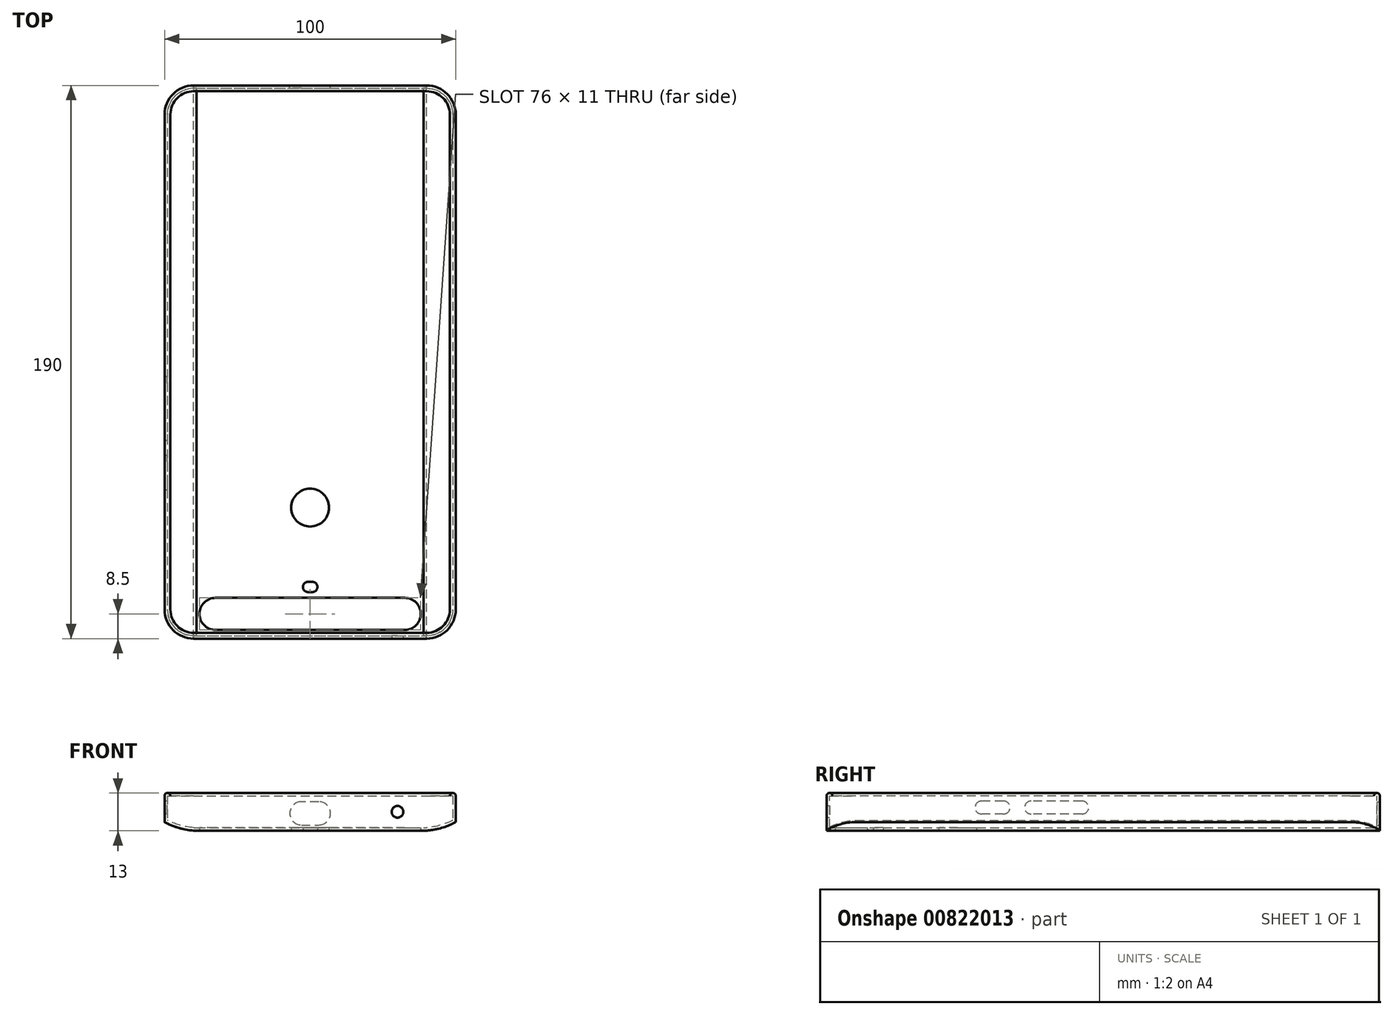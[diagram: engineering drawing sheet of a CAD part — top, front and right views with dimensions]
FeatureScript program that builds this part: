
annotation { "Feature Type Name" : "Feature", "Feature Type Description" : "" }
export const myFeature = defineFeature(function(context is Context, id is Id, definition is map)
    precondition{}
    {
        {
            var Q0;
            Q0=qCreatedBy(makeId("Top.planeOp"),FACE);
            var sketch = newSketch(context, id + "F0", { "sketchPlane" : qUnion([Q0])});
            skLineSegment(sketch, "E0.bottom", {"start": v(-40, 95) * mm, "end": v(40, 95) * mm});
            skLineSegment(sketch, "E0.top", {"start": v(-40, -95) * mm, "end": v(40, -95) * mm});
            skLineSegment(sketch, "E0.left", {"start": v(-50, 85) * mm, "end": v(-50, -85) * mm});
            skLineSegment(sketch, "E0.right", {"start": v(50, 85) * mm, "end": v(50, -85) * mm});
            skPoint(sketch, "E1.visualSharp", {"position": v(-50, 95) * mm});
            skArc(sketch, "E1.filletArc", {"start": v(-40, 95) * mm, "mid": v(-47.07, 92.07) * mm, "end": v(-50, 85) * mm});
            skPoint(sketch, "E2.visualSharp", {"position": v(50, 95) * mm});
            skArc(sketch, "E2.filletArc", {"start": v(50, 85) * mm, "mid": v(47.07, 92.07) * mm, "end": v(40, 95) * mm});
            skPoint(sketch, "E3.visualSharp", {"position": v(50, -95) * mm});
            skArc(sketch, "E3.filletArc", {"start": v(40, -95) * mm, "mid": v(47.07, -92.07) * mm, "end": v(50, -85) * mm});
            skPoint(sketch, "E4.visualSharp", {"position": v(-50, -95) * mm});
            skArc(sketch, "E4.filletArc", {"start": v(-50, -85) * mm, "mid": v(-47.07, -92.07) * mm, "end": v(-40, -95) * mm});
            skLineSegment(sketch, "E5", {"start": v(0, 95) * mm, "end": v(0, -95) * mm, "construction": true});
            skLineSegment(sketch, "E6", {"start": v(-50, 0) * mm, "end": v(50, 0) * mm, "construction": true});
            skSolve(sketch);
        }
        {
            var Q0;
            Q0=makeQuery(id+"F0.imprint","IMPRINT",FACE,{"disambiguationData":[TD([[makeQuery(id+"F0.imprint","IMPRINT",EDGE,{"derivedFrom":sQuery(id+"F0.wireOp",EDGE,"E0.bottom")}),-1.0]])]});
            extrude(context, id + "F1", {"entities" : qUnion([Q0]), "depth" : 12 * mm});
        }
        {
            var Q0;
            Q0=makeQuery(id+"F1.opExtrude","SWEPT_FACE",FACE,{"disambiguationData":[OSD([sQuery(id+"F0.wireOp",EDGE,"E0.bottom")])]});
            var sketch = newSketch(context, id + "F2", { "sketchPlane" : qUnion([Q0])});
            skLineSegment(sketch, "E7.0", {"start": v(-50, 0) * mm, "end": v(-38, 0) * mm});
            skLineSegment(sketch, "E8.0", {"start": v(-50, 3) * mm, "end": v(-50, 0) * mm});
            skArc(sketch, "E9", {"start": v(-50, 3) * mm, "mid": v(-44.19, 0.75) * mm, "end": v(-38, 0) * mm});
            skArc(sketch, "E10.MirrorCS", {"start": v(50, 3) * mm, "mid": v(44.19, 0.75) * mm, "end": v(38, 0) * mm});
            skLineSegment(sketch, "E11.MirrorCS", {"start": v(50, 3) * mm, "end": v(50, 0) * mm});
            skLineSegment(sketch, "E12.MirrorCS", {"start": v(50, 0) * mm, "end": v(38, 0) * mm});
            skSolve(sketch);
        }
        {
            var Q0;
            {var subQ3=sQuery(id+"F2.wireOp",EDGE,"E8.0");Q0=makeQuery(id+"F2.imprint","IMPRINT",FACE,{"disambiguationData":[TD([[makeQuery(id+"F2.imprint","IMPRINT",EDGE,{"derivedFrom":subQ3}),1.0]])]});}
            var Q1;
            {var subQ0=sQuery(id+"F2.wireOp",EDGE,"E11.MirrorCS");Q1=makeQuery(id+"F2.imprint","IMPRINT",FACE,{"disambiguationData":[TD([[makeQuery(id+"F2.imprint","IMPRINT",EDGE,{"derivedFrom":subQ0}),-1.0]])]});}
            extrude(context, id + "F3", {"entities" : qUnion([Q0, Q1]), "operationType" : NewBodyOperationType.REMOVE, "endBound" : BoundingType.THROUGH_ALL, "oppositeDirection" : true, "depth" : 25 * mm});
        }
        {
            var Q0;
            Q0=makeQuery(id+"F1.opExtrude","CAP_FACE",FACE,{"disambiguationData":[OSD([sQuery(id+"F0.wireOp",EDGE,"E0.bottom"),sQuery(id+"F0.wireOp",EDGE,"E0.top"),sQuery(id+"F0.wireOp",EDGE,"E0.left"),sQuery(id+"F0.wireOp",EDGE,"E0.right"),sQuery(id+"F0.wireOp",EDGE,"E1.filletArc"),sQuery(id+"F0.wireOp",EDGE,"E2.filletArc"),sQuery(id+"F0.wireOp",EDGE,"E3.filletArc"),sQuery(id+"F0.wireOp",EDGE,"E4.filletArc")])],"isStart":false});
            shell(context, id + "F4", {"entities" : qUnion([Q0]), "thickness" : 1 * mm});
        }
        {
            var Q0;
            Q0=makeQuery(id+"F1.opExtrude","CAP_FACE",FACE,{"disambiguationData":[OSD([sQuery(id+"F0.wireOp",EDGE,"E0.bottom"),sQuery(id+"F0.wireOp",EDGE,"E0.top"),sQuery(id+"F0.wireOp",EDGE,"E0.left"),sQuery(id+"F0.wireOp",EDGE,"E0.right"),sQuery(id+"F0.wireOp",EDGE,"E1.filletArc"),sQuery(id+"F0.wireOp",EDGE,"E2.filletArc"),sQuery(id+"F0.wireOp",EDGE,"E3.filletArc"),sQuery(id+"F0.wireOp",EDGE,"E4.filletArc")])],"isStart":false});
            var sketch = newSketch(context, id + "F5", { "sketchPlane" : qUnion([Q0])});
            skLineSegment(sketch, "E13.0", {"start": v(-40, 95) * mm, "end": v(40, 95) * mm});
            skArc(sketch, "E14.0", {"start": v(-40, 95) * mm, "mid": v(-47.07, 92.07) * mm, "end": v(-50, 85) * mm});
            skLineSegment(sketch, "E15.0", {"start": v(-50, 85) * mm, "end": v(-50, -85) * mm});
            skArc(sketch, "E16.0", {"start": v(50, 85) * mm, "mid": v(47.07, 92.07) * mm, "end": v(40, 95) * mm});
            skLineSegment(sketch, "E17.0", {"start": v(50, 85) * mm, "end": v(50, -85) * mm});
            skArc(sketch, "E18.0", {"start": v(-50, -85) * mm, "mid": v(-47.07, -92.07) * mm, "end": v(-40, -95) * mm});
            skLineSegment(sketch, "E19.0", {"start": v(-40, -95) * mm, "end": v(40, -95) * mm});
            skArc(sketch, "E20.0", {"start": v(40, -95) * mm, "mid": v(47.07, -92.07) * mm, "end": v(50, -85) * mm});
            skLineSegment(sketch, "E21.0", {"start": v(-40, 93) * mm, "end": v(40, 93) * mm});
            skArc(sketch, "E21.1", {"start": v(48, 85) * mm, "mid": v(45.66, 90.66) * mm, "end": v(40, 93) * mm});
            skArc(sketch, "E21.2", {"start": v(-40, 93) * mm, "mid": v(-45.66, 90.66) * mm, "end": v(-48, 85) * mm});
            skLineSegment(sketch, "E21.3", {"start": v(48, 85) * mm, "end": v(48, -85) * mm});
            skLineSegment(sketch, "E21.4", {"start": v(-48, 85) * mm, "end": v(-48, -85) * mm});
            skArc(sketch, "E21.5", {"start": v(-48, -85) * mm, "mid": v(-45.66, -90.66) * mm, "end": v(-40, -93) * mm});
            skLineSegment(sketch, "E21.6", {"start": v(-40, -93) * mm, "end": v(40, -93) * mm});
            skArc(sketch, "E21.7", {"start": v(40, -93) * mm, "mid": v(45.66, -90.66) * mm, "end": v(48, -85) * mm});
            skSolve(sketch);
        }
        {
            var Q0;
            Q0=qSketchRegion(id+"F5",true);
            extrude(context, id + "F6", {"entities" : qUnion([Q0]), "operationType" : NewBodyOperationType.ADD, "depth" : 1 * mm});
        }
        {
            var Q0;
            Q0=makeQuery(id+"F1.opExtrude","CAP_FACE",FACE,{"disambiguationData":[OSD([sQuery(id+"F0.wireOp",EDGE,"E0.bottom"),sQuery(id+"F0.wireOp",EDGE,"E0.top"),sQuery(id+"F0.wireOp",EDGE,"E0.left"),sQuery(id+"F0.wireOp",EDGE,"E0.right"),sQuery(id+"F0.wireOp",EDGE,"E1.filletArc"),sQuery(id+"F0.wireOp",EDGE,"E2.filletArc"),sQuery(id+"F0.wireOp",EDGE,"E3.filletArc"),sQuery(id+"F0.wireOp",EDGE,"E4.filletArc")])],"isStart":true});
            var sketch = newSketch(context, id + "F7", { "sketchPlane" : qUnion([Q0])});
            skLineSegment(sketch, "E22", {"start": v(-40, 95) * mm, "end": v(-40, -95) * mm, "construction": true});
            skLineSegment(sketch, "E23", {"start": v(40, 95) * mm, "end": v(40, -95) * mm, "construction": true});
            skCircle(sketch, "E24", {"center": v(0, 50) * mm, "radius": 6.5 * mm});
            skLineSegment(sketch, "E25", {"start": v(-38, 92) * mm, "end": v(-32.5, 92) * mm, "construction": true});
            skLineSegment(sketch, "E26", {"start": v(-38, 81) * mm, "end": v(-32.5, 81) * mm, "construction": true});
            skLineSegment(sketch, "E27", {"start": v(0, 79) * mm, "end": v(0, 95) * mm, "construction": true});
            skArc(sketch, "E28", {"start": v(-32.5, 92) * mm, "mid": v(-38, 86.5) * mm, "end": v(-32.5, 81) * mm});
            skArc(sketch, "E29", {"start": v(32.5, 81) * mm, "mid": v(38, 86.5) * mm, "end": v(32.5, 92) * mm});
            skLineSegment(sketch, "E30", {"start": v(38, 92) * mm, "end": v(38, 81) * mm, "construction": true});
            skLineSegment(sketch, "E31", {"start": v(-38, 92) * mm, "end": v(-38, 81) * mm, "construction": true});
            skLineSegment(sketch, "E32", {"start": v(-32.5, 92) * mm, "end": v(32.5, 92) * mm});
            skLineSegment(sketch, "E33", {"start": v(32.5, 81) * mm, "end": v(-32.5, 81) * mm});
            skLineSegment(sketch, "E34.trimOffspring", {"start": v(32.5, 92) * mm, "end": v(38, 92) * mm, "construction": true});
            skLineSegment(sketch, "E35.trimOffspring", {"start": v(32.5, 81) * mm, "end": v(38, 81) * mm, "construction": true});
            skLineSegment(sketch, "E36", {"start": v(-2.5, 79) * mm, "end": v(-0.75, 79) * mm, "construction": true});
            skLineSegment(sketch, "E37", {"start": v(-2.5, 75.5) * mm, "end": v(-0.75, 75.5) * mm, "construction": true});
            skLineSegment(sketch, "E38", {"start": v(-2.5, 79) * mm, "end": v(-2.5, 75.5) * mm, "construction": true});
            skLineSegment(sketch, "E39", {"start": v(2.5, 79) * mm, "end": v(2.5, 75.5) * mm, "construction": true});
            skArc(sketch, "E40", {"start": v(-0.75, 79) * mm, "mid": v(-2.5, 77.25) * mm, "end": v(-0.75, 75.5) * mm});
            skArc(sketch, "E41", {"start": v(0.75, 75.5) * mm, "mid": v(2.5, 77.25) * mm, "end": v(0.75, 79) * mm});
            skLineSegment(sketch, "E42", {"start": v(-0.75, 75.5) * mm, "end": v(0.75, 75.5) * mm});
            skLineSegment(sketch, "E43", {"start": v(-0.75, 79) * mm, "end": v(0.75, 79) * mm});
            skLineSegment(sketch, "E44.trimOffspring", {"start": v(0.75, 79) * mm, "end": v(2.5, 79) * mm, "construction": true});
            skLineSegment(sketch, "E45.trimOffspring", {"start": v(0.75, 75.5) * mm, "end": v(2.5, 75.5) * mm, "construction": true});
            skLineSegment(sketch, "E46", {"start": v(-50, 81) * mm, "end": v(50, 81) * mm});
            skArc(sketch, "E47.0", {"start": v(-50, 85) * mm, "mid": v(-47.07, 92.07) * mm, "end": v(-40, 95) * mm});
            skPoint(sketch, "E48.0", {"position": v(47.07, 92.07) * mm});
            skArc(sketch, "E49.0", {"start": v(40, 95) * mm, "mid": v(47.07, 92.07) * mm, "end": v(50, 85) * mm});
            skLineSegment(sketch, "E50", {"start": v(50, 85) * mm, "end": v(50, 81) * mm});
            skLineSegment(sketch, "E51", {"start": v(-50, 81) * mm, "end": v(-50, 85) * mm});
            skLineSegment(sketch, "E52", {"start": v(40, 95) * mm, "end": v(-40, 95) * mm});
            skSolve(sketch);
        }
        {
            var Q0;
            {var subQ0=sQuery(id+"F7.wireOp",EDGE,"E28");Q0=makeQuery(id+"F7.imprint","IMPRINT",FACE,{"disambiguationData":[TD([[makeQuery(id+"F7.imprint","IMPRINT",EDGE,{"derivedFrom":subQ0}),1.0]])]});}
            var Q1;
            Q1=makeQuery(id+"F7.imprint","IMPRINT",FACE,{"disambiguationData":[TD([[makeQuery(id+"F7.imprint","IMPRINT",EDGE,{"derivedFrom":sQuery(id+"F7.wireOp",EDGE,"E40")}),1.0]])]});
            var Q2;
            Q2=makeQuery(id+"F7.imprint","IMPRINT",FACE,{"disambiguationData":[TD([[makeQuery(id+"F7.imprint","IMPRINT",EDGE,{"derivedFrom":sQuery(id+"F7.wireOp",EDGE,"E24")}),1.0]])]});
            extrude(context, id + "F8", {"entities" : qUnion([Q0, Q1, Q2]), "operationType" : NewBodyOperationType.REMOVE, "endBound" : BoundingType.THROUGH_ALL, "oppositeDirection" : true, "depth" : 25 * mm});
        }
        {
            var Q0;
            Q0=makeQuery(id+"F6.boolean.opBoolean","MERGE",FACE,{"derivedFrom":[makeQuery(id+"F1.opExtrude","SWEPT_FACE",FACE,{"disambiguationData":[OSD([sQuery(id+"F0.wireOp",EDGE,"E0.top")])]}),makeQuery(id+"F6.opExtrude","SWEPT_FACE",FACE,{"disambiguationData":[OSD([sQuery(id+"F5.wireOp",EDGE,"E19.0")])]})]});
            var sketch = newSketch(context, id + "F9", { "sketchPlane" : qUnion([Q0])});
            skCircle(sketch, "E53", {"center": v(30, 6.54) * mm, "radius": 2 * mm});
            skLineSegment(sketch, "E54", {"start": v(30, 6.54) * mm, "end": v(40, 6.54) * mm, "construction": true});
            skSolve(sketch);
        }
        {
            var Q0;
            Q0=makeQuery(id+"F9.imprint","IMPRINT",FACE,{"disambiguationData":[TD([[makeQuery(id+"F9.imprint","IMPRINT",EDGE,{"derivedFrom":sQuery(id+"F9.wireOp",EDGE,"E53")}),1.0]])]});
            extrude(context, id + "F10", {"entities" : qUnion([Q0]), "operationType" : NewBodyOperationType.REMOVE, "endBound" : BoundingType.UP_TO_NEXT, "oppositeDirection" : true, "depth" : 25 * mm});
        }
        {
            var Q0;
            Q0=makeQuery(id+"F6.boolean.opBoolean","MERGE",FACE,{"derivedFrom":[makeQuery(id+"F1.opExtrude","SWEPT_FACE",FACE,{"disambiguationData":[OSD([sQuery(id+"F0.wireOp",EDGE,"E0.bottom")])]}),makeQuery(id+"F6.opExtrude","SWEPT_FACE",FACE,{"disambiguationData":[OSD([sQuery(id+"F5.wireOp",EDGE,"E13.0")])]})]});
            var sketch = newSketch(context, id + "F11", { "sketchPlane" : qUnion([Q0])});
            skArc(sketch, "E55", {"start": v(-3, 10) * mm, "mid": v(-7, 6) * mm, "end": v(-3, 2) * mm});
            skArc(sketch, "E56", {"start": v(3, 2) * mm, "mid": v(7, 6) * mm, "end": v(3, 10) * mm});
            skLineSegment(sketch, "E57", {"start": v(-3, 10) * mm, "end": v(3, 10) * mm});
            skLineSegment(sketch, "E58", {"start": v(3, 2) * mm, "end": v(-3, 2) * mm});
            skLineSegment(sketch, "E59", {"start": v(-3, 6) * mm, "end": v(3, 6) * mm, "construction": true});
            skLineSegment(sketch, "E60", {"start": v(0, 6) * mm, "end": v(0, 0) * mm, "construction": true});
            skSolve(sketch);
        }
        {
            var Q0;
            Q0=makeQuery(id+"F11.imprint","IMPRINT",FACE,{"disambiguationData":[TD([[makeQuery(id+"F11.imprint","IMPRINT",EDGE,{"derivedFrom":sQuery(id+"F11.wireOp",EDGE,"E55")}),1.0]])]});
            extrude(context, id + "F12", {"entities" : qUnion([Q0]), "operationType" : NewBodyOperationType.REMOVE, "endBound" : BoundingType.UP_TO_NEXT, "oppositeDirection" : true, "depth" : 25 * mm});
        }
        {
            var Q0;
            Q0=makeQuery(id+"F6.boolean.opBoolean","MERGE",FACE,{"derivedFrom":[makeQuery(id+"F1.opExtrude","SWEPT_FACE",FACE,{"disambiguationData":[OSD([sQuery(id+"F0.wireOp",EDGE,"E0.left")])]}),makeQuery(id+"F6.opExtrude","SWEPT_FACE",FACE,{"disambiguationData":[OSD([sQuery(id+"F5.wireOp",EDGE,"E15.0")])]})]});
            var sketch = newSketch(context, id + "F13", { "sketchPlane" : qUnion([Q0])});
            skLineSegment(sketch, "E61", {"start": v(38, 10.22) * mm, "end": v(38, 5.78) * mm, "construction": true});
            skLineSegment(sketch, "E62", {"start": v(34.22, 10.22) * mm, "end": v(41.78, 10.22) * mm});
            skLineSegment(sketch, "E63", {"start": v(16, 10.22) * mm, "end": v(16, 5.78) * mm, "construction": true});
            skLineSegment(sketch, "E64", {"start": v(7.22, 10.22) * mm, "end": v(24.78, 10.22) * mm});
            skLineSegment(sketch, "E65", {"start": v(7.22, 5.78) * mm, "end": v(24.78, 5.78) * mm});
            skLineSegment(sketch, "E66", {"start": v(34.22, 5.78) * mm, "end": v(41.78, 5.78) * mm});
            skLineSegment(sketch, "E67", {"start": v(38, 8) * mm, "end": v(85, 8) * mm, "construction": true});
            skLineSegment(sketch, "E68", {"start": v(38, 8) * mm, "end": v(16, 8) * mm, "construction": true});
            skArc(sketch, "E69", {"start": v(7.22, 10.22) * mm, "mid": v(5, 8) * mm, "end": v(7.22, 5.78) * mm});
            skLineSegment(sketch, "E70", {"start": v(5, 10.22) * mm, "end": v(5, 5.78) * mm, "construction": true});
            skArc(sketch, "E71", {"start": v(24.78, 5.78) * mm, "mid": v(27, 8) * mm, "end": v(24.78, 10.22) * mm});
            skLineSegment(sketch, "E72", {"start": v(27, 10.22) * mm, "end": v(27, 5.78) * mm, "construction": true});
            skLineSegment(sketch, "E73", {"start": v(5, 5.78) * mm, "end": v(7.22, 5.78) * mm, "construction": true});
            skLineSegment(sketch, "E74", {"start": v(5, 10.22) * mm, "end": v(7.22, 10.22) * mm, "construction": true});
            skLineSegment(sketch, "E75", {"start": v(24.78, 10.22) * mm, "end": v(27, 10.22) * mm, "construction": true});
            skLineSegment(sketch, "E76", {"start": v(27, 5.78) * mm, "end": v(24.78, 5.78) * mm, "construction": true});
            skArc(sketch, "E77", {"start": v(34.22, 10.22) * mm, "mid": v(32, 8) * mm, "end": v(34.22, 5.78) * mm});
            skArc(sketch, "E78", {"start": v(41.78, 5.78) * mm, "mid": v(44, 8) * mm, "end": v(41.78, 10.22) * mm});
            skLineSegment(sketch, "E79", {"start": v(44, 10.22) * mm, "end": v(44, 5.78) * mm, "construction": true});
            skLineSegment(sketch, "E80", {"start": v(32, 10.22) * mm, "end": v(32, 5.78) * mm, "construction": true});
            skLineSegment(sketch, "E81", {"start": v(32, 10.22) * mm, "end": v(34.22, 10.22) * mm, "construction": true});
            skLineSegment(sketch, "E82", {"start": v(32, 5.78) * mm, "end": v(34.22, 5.78) * mm, "construction": true});
            skLineSegment(sketch, "E83", {"start": v(41.78, 5.78) * mm, "end": v(44, 5.78) * mm, "construction": true});
            skLineSegment(sketch, "E84", {"start": v(41.78, 10.22) * mm, "end": v(44, 10.22) * mm, "construction": true});
            skSolve(sketch);
        }
        {
            var Q0;
            Q0=qSketchRegion(id+"F13",true);
            extrude(context, id + "F14", {"entities" : qUnion([Q0]), "operationType" : NewBodyOperationType.REMOVE, "endBound" : BoundingType.UP_TO_NEXT, "oppositeDirection" : true, "depth" : 25 * mm});
        }
        {
            var Q0;
            Q0=makeQuery(id+"F8.boolean.opBoolean","COPY",EDGE,{"derivedFrom":makeQuery(id+"F8.opExtrude","CAP_EDGE",EDGE,{"disambiguationData":[OSD([sQuery(id+"F7.wireOp",EDGE,"E24")])],"isStart":true})});
            var Q1;
            Q1=makeQuery(id+"F8.boolean.opBoolean","COPY",EDGE,{"derivedFrom":makeQuery(id+"F8.opExtrude","CAP_EDGE",EDGE,{"disambiguationData":[OSD([sQuery(id+"F7.wireOp",EDGE,"CuEtsgBI-tdXd-w1cR-YagW-tM3tnziSwPTY")])],"isStart":true})});
            var Q2;
            Q2=makeQuery(id+"F8.boolean.opBoolean","COPY",EDGE,{"derivedFrom":makeQuery(id+"F8.opExtrude","CAP_EDGE",EDGE,{"disambiguationData":[OSD([sQuery(id+"F7.wireOp",EDGE,"EOcf2Z3M-5h8k-OmuV-YNXX-lS85Hog08SEh")])],"isStart":true})});
            var Q3;
            Q3=makeQuery(id+"F10.boolean.opBoolean","COPY",EDGE,{"derivedFrom":makeQuery(id+"F10.opExtrude","CAP_EDGE",EDGE,{"disambiguationData":[OSD([sQuery(id+"F9.wireOp",EDGE,"E53")])],"isStart":true})});
            var Q4;
            Q4=makeQuery(id+"F6.opExtrude","CAP_FACE",FACE,{"disambiguationData":[OSD([sQuery(id+"F5.wireOp",EDGE,"E13.0"),sQuery(id+"F5.wireOp",EDGE,"E14.0"),sQuery(id+"F5.wireOp",EDGE,"E15.0"),sQuery(id+"F5.wireOp",EDGE,"E16.0"),sQuery(id+"F5.wireOp",EDGE,"E17.0"),sQuery(id+"F5.wireOp",EDGE,"E18.0"),sQuery(id+"F5.wireOp",EDGE,"E19.0"),sQuery(id+"F5.wireOp",EDGE,"E20.0"),sQuery(id+"F5.wireOp",EDGE,"E21.0"),sQuery(id+"F5.wireOp",EDGE,"E21.1"),sQuery(id+"F5.wireOp",EDGE,"E21.2"),sQuery(id+"F5.wireOp",EDGE,"E21.3"),sQuery(id+"F5.wireOp",EDGE,"E21.4"),sQuery(id+"F5.wireOp",EDGE,"E21.5"),sQuery(id+"F5.wireOp",EDGE,"E21.6"),sQuery(id+"F5.wireOp",EDGE,"E21.7")])],"isStart":false});
            var Q5;
            Q5=makeQuery(id+"F8.boolean.opBoolean","COPY",EDGE,{"derivedFrom":makeQuery(id+"F8.opExtrude","CAP_EDGE",EDGE,{"disambiguationData":[OSD([sQuery(id+"F7.wireOp",EDGE,"fg4qu1gz-vClW-fxv8-D8oB-zsSMNXw7GYdb")])],"isStart":true})});
            var Q6;
            Q6=makeQuery(id+"F8.boolean.opBoolean","COPY",EDGE,{"derivedFrom":makeQuery(id+"F8.opExtrude","CAP_EDGE",EDGE,{"disambiguationData":[OSD([sQuery(id+"F7.wireOp",EDGE,"SX1fq37g-197b-jUmr-uY5f-YUkrL5FpuJ1j")])],"isStart":true})});
            var Q7;
            Q7=makeQuery(id+"F12.boolean.opBoolean","COPY",EDGE,{"derivedFrom":makeQuery(id+"F12.opExtrude","CAP_EDGE",EDGE,{"disambiguationData":[OSD([sQuery(id+"F11.wireOp",EDGE,"E55")])],"isStart":true})});
            var Q8;
            Q8=makeQuery(id+"F12.boolean.opBoolean","COPY",EDGE,{"derivedFrom":makeQuery(id+"F12.opExtrude","CAP_EDGE",EDGE,{"disambiguationData":[OSD([sQuery(id+"F11.wireOp",EDGE,"E57")])],"isStart":true})});
            var Q9;
            Q9=makeQuery(id+"F8.boolean.opBoolean","COPY",EDGE,{"derivedFrom":makeQuery(id+"F8.opExtrude","CAP_EDGE",EDGE,{"disambiguationData":[OSD([sQuery(id+"F7.wireOp",EDGE,"E40")])],"isStart":true})});
            var Q10;
            Q10=makeQuery(id+"F8.boolean.opBoolean","COPY",EDGE,{"derivedFrom":makeQuery(id+"F8.opExtrude","CAP_EDGE",EDGE,{"disambiguationData":[OSD([sQuery(id+"F7.wireOp",EDGE,"E32")])],"isStart":true})});
            var Q11;
            Q11=makeQuery(id+"F14.boolean.opBoolean","COPY",EDGE,{"derivedFrom":makeQuery(id+"F14.opExtrude","CAP_EDGE",EDGE,{"disambiguationData":[OSD([sQuery(id+"F13.wireOp",EDGE,"E77")])],"isStart":true})});
            var Q12;
            Q12=makeQuery(id+"F14.boolean.opBoolean","COPY",EDGE,{"derivedFrom":makeQuery(id+"F14.opExtrude","CAP_EDGE",EDGE,{"disambiguationData":[OSD([sQuery(id+"F13.wireOp",EDGE,"E71")])],"isStart":true})});
            fillet(context, id + "F15", {"entities" : qUnion([Q0, Q1, Q2, Q3, Q4, Q5, Q6, Q7, Q8, Q9, Q10, Q11, Q12]), "radius" : 1 * mm, "tangentPropagation" : true, "allowEdgeOverflow" : false});
        }
    });
